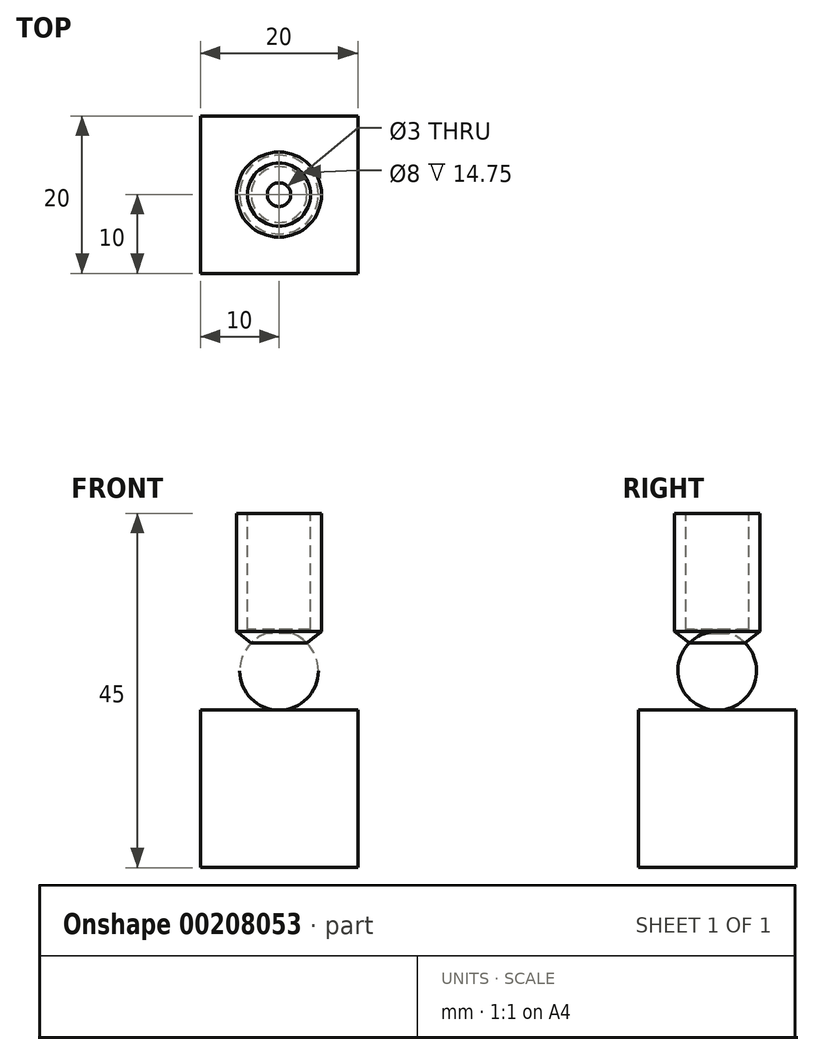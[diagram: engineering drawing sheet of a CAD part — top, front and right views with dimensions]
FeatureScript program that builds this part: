
annotation { "Feature Type Name" : "Feature", "Feature Type Description" : "" }
export const myFeature = defineFeature(function(context is Context, id is Id, definition is map)
    precondition{}
    {
        {
            var Q0;
            Q0=qCreatedBy(makeId("Front.planeOp"),FACE);
            var sketch = newSketch(context, id + "F0", { "sketchPlane" : qUnion([Q0])});
            skLineSegment(sketch, "E0", {"start": v(0, 0) * mm, "end": v(-3.54, 0) * mm, "construction": true});
            skLineSegment(sketch, "E1", {"start": v(-3.54, 1.46) * mm, "end": v(0, 1.46) * mm});
            skLineSegment(sketch, "E2", {"start": v(0, 0) * mm, "end": v(0, 1.46) * mm, "construction": true});
            skLineSegment(sketch, "E3", {"start": v(-3.54, 0) * mm, "end": v(0, -3.54) * mm, "construction": true});
            skLineSegment(sketch, "E4", {"start": v(0, 0) * mm, "end": v(0, -3.54) * mm, "construction": true});
            skLineSegment(sketch, "E5.bottom", {"start": v(-5.4, 16.46) * mm, "end": v(-4, 16.46) * mm});
            skLineSegment(sketch, "E5.top", {"start": v(-5.4, 1.46) * mm, "end": v(-4, 1.46) * mm});
            skLineSegment(sketch, "E5.left", {"start": v(-5.4, 16.46) * mm, "end": v(-5.4, 1.46) * mm});
            skLineSegment(sketch, "E5.right", {"start": v(-4, 16.46) * mm, "end": v(-4, 1.46) * mm});
            skLineSegment(sketch, "E6", {"start": v(-5.4, 1.46) * mm, "end": v(-3.54, 0) * mm});
            skLineSegment(sketch, "E7", {"start": v(-3.54, 1.46) * mm, "end": v(-3.54, 0) * mm});
            skCircle(sketch, "E8", {"center": v(0, -3.54) * mm, "radius": 5 * mm});
            skLineSegment(sketch, "E9", {"start": v(-1.5, 1.46) * mm, "end": v(-1.5, 1.23) * mm});
            skLineSegment(sketch, "E10", {"start": v(-1.5, 1.46) * mm, "end": v(-1.5, 1.71) * mm});
            skLineSegment(sketch, "E11", {"start": v(-1.5, 1.71) * mm, "end": v(-4, 1.71) * mm});
            skLineSegment(sketch, "E12", {"start": v(0, -3.54) * mm, "end": v(5, -3.54) * mm});
            skLineSegment(sketch, "E13", {"start": v(0, -3.54) * mm, "end": v(-5, -3.54) * mm});
            skLineSegment(sketch, "E14.bottom", {"start": v(-10, -8.54) * mm, "end": v(10, -8.54) * mm});
            skLineSegment(sketch, "E14.top", {"start": v(-10, -28.54) * mm, "end": v(10, -28.54) * mm});
            skLineSegment(sketch, "E14.left", {"start": v(-10, -8.54) * mm, "end": v(-10, -28.54) * mm});
            skLineSegment(sketch, "E14.right", {"start": v(10, -8.54) * mm, "end": v(10, -28.54) * mm});
            skPoint(sketch, "E15", {"position": v(0, -8.54) * mm});
            skLineSegment(sketch, "E16", {"start": v(0, -3.54) * mm, "end": v(0, -8.54) * mm, "construction": true});
            skSolve(sketch);
        }
        {
            var Q0;
            {var subQ1=sQuery(id+"F0.wireOp",EDGE,"E7");Q0=makeQuery(id+"F0.imprint","IMPRINT",FACE,{"disambiguationData":[TD([[makeQuery(id+"F0.imprint","IMPRINT",EDGE,{"derivedFrom":subQ1}),1.0]])]});}
            var Q1;
            {var subQ5=sQuery(id+"F0.wireOp",EDGE,"E5.bottom");Q1=makeQuery(id+"F0.imprint","IMPRINT",FACE,{"disambiguationData":[TD([[makeQuery(id+"F0.imprint","IMPRINT",EDGE,{"derivedFrom":subQ5}),-1.0]])]});}
            var Q2;
            {var subQ0=sQuery(id+"F0.wireOp",EDGE,"E6");Q2=makeQuery(id+"F0.imprint","IMPRINT",FACE,{"disambiguationData":[TD([[makeQuery(id+"F0.imprint","IMPRINT",EDGE,{"derivedFrom":subQ0}),1.0]])]});}
            var Q3;
            {var subQ3=sQuery(id+"F0.wireOp",EDGE,"E10");Q3=makeQuery(id+"F0.imprint","IMPRINT",FACE,{"disambiguationData":[TD([[makeQuery(id+"F0.imprint","IMPRINT",EDGE,{"derivedFrom":subQ3}),1.0]])]});}
            var Q4;
            Q4=sQuery(id+"F0.wireOp",EDGE,"E2");
            revolve(context, id + "F1", {"entities" : qUnion([Q0, Q1, Q2, Q3]), "axis" : qUnion([Q4]), "revolveType" : RevolveType.FULL, "oppositeDirection" : true});
        }
        {
            var Q0;
            {var subQ0=sQuery(id+"F0.wireOp",EDGE,"E12");Q0=makeQuery(id+"F0.imprint","IMPRINT",FACE,{"disambiguationData":[TD([[makeQuery(id+"F0.imprint","IMPRINT",EDGE,{"derivedFrom":subQ0}),-1.0]])]});}
            var Q1;
            Q1=sQuery(id+"F0.wireOp",EDGE,"E13");
            revolve(context, id + "F2", {"entities" : qUnion([Q0]), "axis" : qUnion([Q1]), "revolveType" : RevolveType.FULL});
        }
        {
            var Q0;
            Q0=makeQuery(id+"F0.imprint","IMPRINT",FACE,{"disambiguationData":[TD([[makeQuery(id+"F0.imprint","IMPRINT",EDGE,{"derivedFrom":sQuery(id+"F0.wireOp",EDGE,"E14.top")}),1.0]])]});
            extrude(context, id + "F3", {"entities" : qUnion([Q0]), "depth" : 20 * mm, "symmetric" : true});
        }
    });
